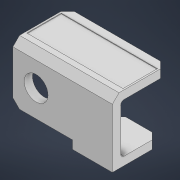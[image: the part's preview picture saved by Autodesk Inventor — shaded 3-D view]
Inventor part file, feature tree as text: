
AUTODESK INVENTOR PART (.ipt)
format: ipt  version: 2021 (Build 250183000, 183)  size: 163,840 bytes
history: native  units: mm
features: sketch x6, extrude x4, fillet x4, hole x1, chamfer x1, emboss x1
ambient origin geometry x8: Origin, YZ Plane, XZ Plane, XY Plane, X Axis, Y Axis, Z Axis, Center Point
bodies: Solid1 (feature_tree)
feature tree (17):
  extrude  "Extrusion1"  Depth=17.3mm
  hole  "Hole1"  [1 undecoded]
  extrude  "Extrusion2"  Depth=8.0mm
  extrude  "Extrusion3"  Depth=12.0mm
  fillet  "Fillet1"  Radius=14.0mm
  fillet  "Fillet2"  Radius=5.5mm
  fillet  "Fillet3"  Radius=1.0mm
  extrude  "Extrusion4"  Depth=0.2mm
  chamfer  "Chamfer2"  Distance=2.5mm
  fillet  "Fillet4"  Radius=14.0mm
  emboss  "Emboss1"
  sketch  "Sketch1"  dims[d0=30.0mm d1=17.3mm]
  sketch  "Sketch2"  dims[d2=2.5mm d3=0.0mm d4=7.0mm]
  sketch  "Sketch3"  dims[d5=7.2mm d6=6.0mm d7=4.0mm d8=2.0mm d9=90.0deg d10=8.0mm d11=20.594885mm d12=8.0mm]
  sketch  "Sketch4"  dims[d13=2.5mm d14=12.0mm d15=14.0mm d16=0.0mm d17=5.5mm d18=1.0mm d19=0.0mm]
  sketch  "Sketch5"  dims[d20=0.3mm d21=0.2mm]
  sketch  "Sketch6"  dims[d22=1.0mm d26=2.5mm d27=14.0mm d28=0.0mm d29=2.0mm d30=2.0mm d31=45.0deg d32=1.0mm d33=10.4mm d34=0.5mm d36=0.5mm d37=2.4mm d38=0.2mm d39=0.0mm]
note: 1 required parameter value undecoded (feature->parameter linkage not recoverable at this tier; creation-order binding heuristic only, values carry confidence <= 0.55)
